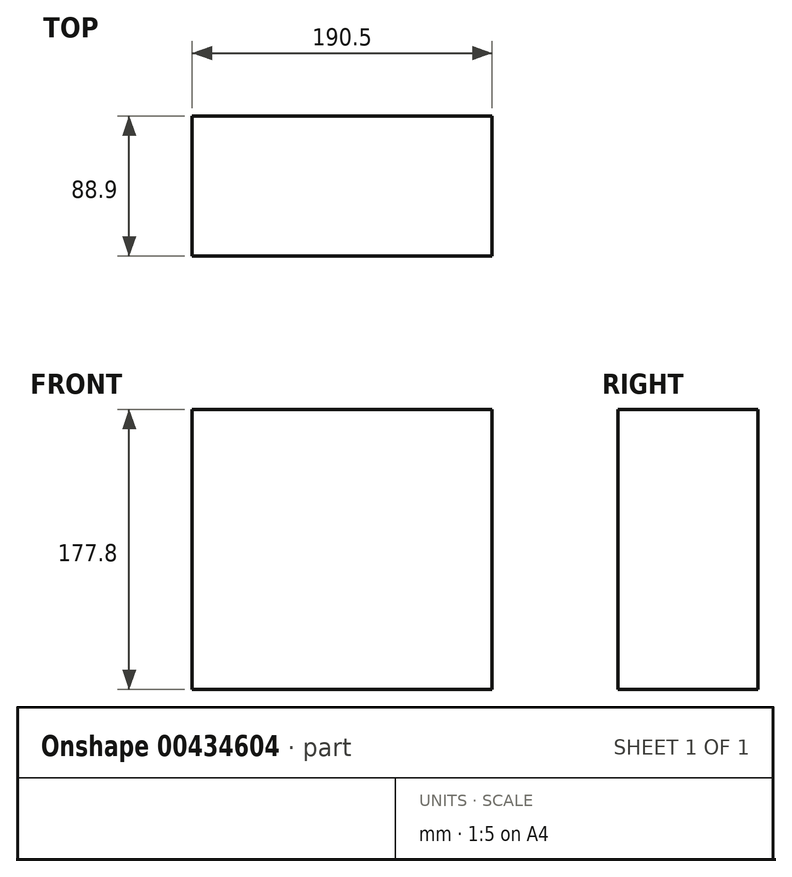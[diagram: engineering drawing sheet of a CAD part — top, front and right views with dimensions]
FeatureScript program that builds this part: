
annotation { "Feature Type Name" : "Feature", "Feature Type Description" : "" }
export const myFeature = defineFeature(function(context is Context, id is Id, definition is map)
    precondition{}
    {
        {
            var Q0;
            Q0=qCreatedBy(makeId("Front.planeOp"),FACE);
            var sketch = newSketch(context, id + "F0", { "sketchPlane" : qUnion([Q0])});
            skLineSegment(sketch, "E0.bottom", {"start": v(-95.25, 88.9) * mm, "end": v(95.25, 88.9) * mm});
            skLineSegment(sketch, "E0.top", {"start": v(-95.25, -88.9) * mm, "end": v(95.25, -88.9) * mm});
            skLineSegment(sketch, "E0.left", {"start": v(-95.25, 88.9) * mm, "end": v(-95.25, -88.9) * mm});
            skLineSegment(sketch, "E0.right", {"start": v(95.25, 88.9) * mm, "end": v(95.25, -88.9) * mm});
            skPoint(sketch, "E0.middle", {"position": v(0, 0) * mm});
            skSolve(sketch);
        }
        {
            var Q0;
            Q0=makeQuery(id+"F0.imprint","IMPRINT",FACE,{"disambiguationData":[TD([[makeQuery(id+"F0.imprint","IMPRINT",EDGE,{"derivedFrom":sQuery(id+"F0.wireOp",EDGE,"E0.bottom")}),-1.0]])]});
            extrude(context, id + "F1", {"entities" : qUnion([Q0]), "depth" : 88.9 * mm});
        }
    });
